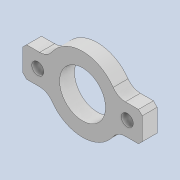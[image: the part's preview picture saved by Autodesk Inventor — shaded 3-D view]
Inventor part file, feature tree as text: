
AUTODESK INVENTOR PART (.ipt)
format: ipt  version: 2020 (Build 240168000, 168)  size: 136,192 bytes
history: native  units: mm
features: thicken_offset x3, sketch x3, other x3, extrude x2, hole x1, chamfer x1, fillet x1, reference x1
ambient origin geometry x8: Origin, YZ Plane, XZ Plane, XY Plane, X Axis, Y Axis, Z Axis, Center Point
bodies: Solid1 (feature_tree)
feature tree (15):
  extrude  "Extrusion1"  Depth=4.0mm
  hole  "Hole1"  [1 undecoded]
  extrude  "Extrusion2"  Depth=2.0mm
  thicken_offset  "Thicken1"
  thicken_offset  "Thicken2"
  chamfer  "Chamfer1"  Distance=2.0mm
  fillet  "Fillet1"  Radius=0.5mm
  thicken_offset  "Thicken3"
  sketch  "Sketch1"  dims[d0=10.0mm d1=4.0mm]
  sketch  "Sketch2"  dims[d2=17.0mm d3=2.0mm d4=0.0mm]
  reference  "Reference1"
  sketch  "Sketch3"  dims[d5=1.6mm d6=6.0mm d7=4.0mm d8=2.0mm d9=90.0deg d10=8.0mm d11=20.594885mm d12=6.0mm d13=2.0mm d14=0.0mm d15=0.5mm d16=0.5mm d17=0.5mm d18=0.5mm d19=0.5mm d20=2.0mm d21=45.0deg d22=2.0mm d23=0.08mm d24=0.08mm]
  parser-record x1  (decoder bookkeeping rows leaked as tree rows — omitted from the tree; the rows remain in map.json)
  other  "tip2_ass_t1.iam"
  other  "cable_holder_1:1"
note: 1 required parameter value undecoded (feature->parameter linkage not recoverable at this tier; creation-order binding heuristic only, values carry confidence <= 0.55)
note: 1 file-system path scrubbed to <path> (originals preserved in map.json)
